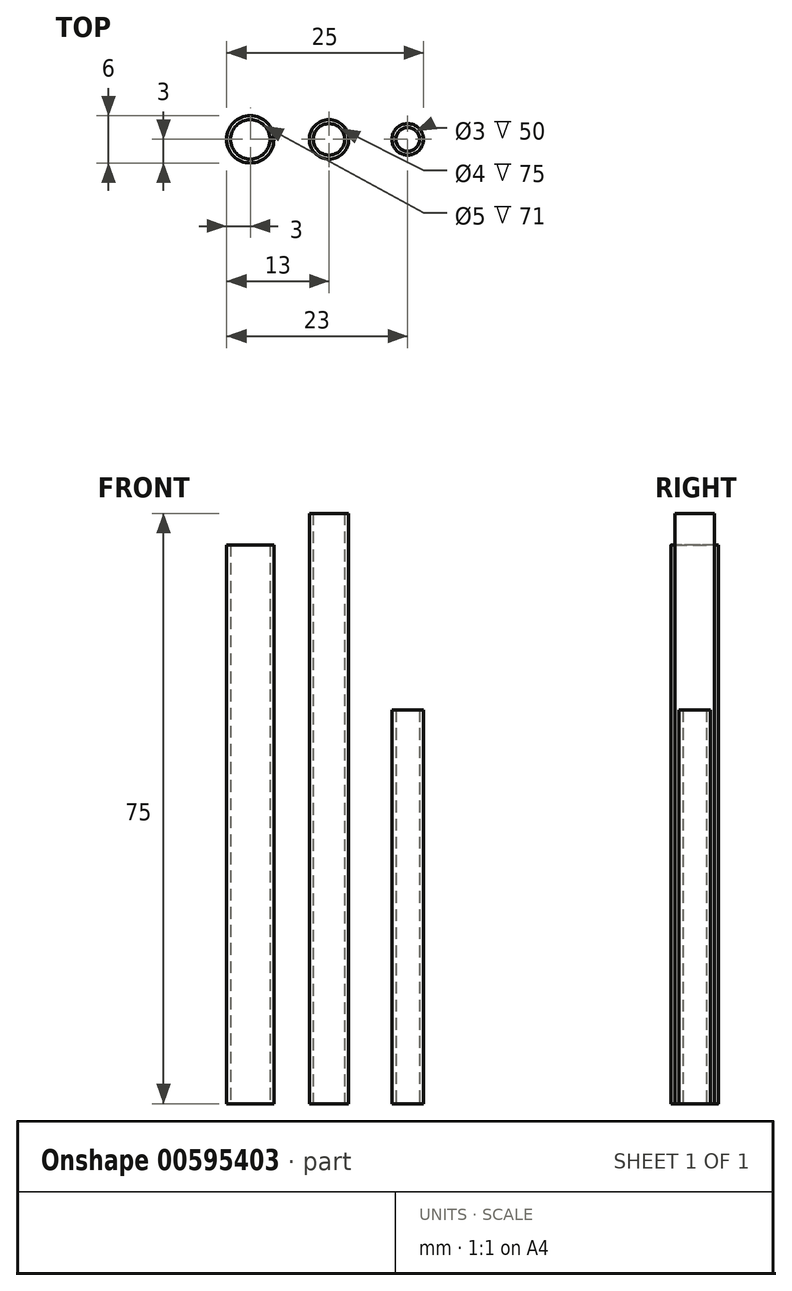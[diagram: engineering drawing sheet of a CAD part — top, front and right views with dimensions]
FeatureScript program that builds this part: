
annotation { "Feature Type Name" : "Feature", "Feature Type Description" : "" }
export const myFeature = defineFeature(function(context is Context, id is Id, definition is map)
    precondition{}
    {
        {
            var Q0;
            Q0=qCreatedBy(makeId("Top.planeOp"),FACE);
            var sketch = newSketch(context, id + "F0", { "sketchPlane" : qUnion([Q0])});
            skCircle(sketch, "E0", {"center": v(-10, 0) * mm, "radius": 3 * mm});
            skCircle(sketch, "E1", {"center": v(-10, 0) * mm, "radius": 2.5 * mm});
            skSolve(sketch);
        }
        {
            var Q0;
            Q0=makeQuery(id+"F0.imprint","IMPRINT",FACE,{"disambiguationData":[TD([[makeQuery(id+"F0.imprint","IMPRINT",EDGE,{"derivedFrom":sQuery(id+"F0.wireOp",EDGE,"E0")}),1.0]])]});
            extrude(context, id + "F1", {"entities" : qUnion([Q0]), "depth" : 71 * mm, "offsetDistance" : 25 * mm});
        }
        {
            var Q0;
            Q0=qCreatedBy(makeId("Top.planeOp"),FACE);
            var sketch = newSketch(context, id + "F2", { "sketchPlane" : qUnion([Q0])});
            skCircle(sketch, "E2", {"center": v(0, 0) * mm, "radius": 2 * mm});
            skCircle(sketch, "E3", {"center": v(0, 0) * mm, "radius": 2.5 * mm});
            skSolve(sketch);
        }
        {
            var Q0;
            Q0=qCreatedBy(makeId("Top.planeOp"),FACE);
            var sketch = newSketch(context, id + "F3", { "sketchPlane" : qUnion([Q0])});
            skCircle(sketch, "E4", {"center": v(10, 0) * mm, "radius": 2 * mm});
            skCircle(sketch, "E5", {"center": v(10, 0) * mm, "radius": 1.5 * mm});
            skSolve(sketch);
        }
        {
            var Q0;
            Q0=makeQuery(id+"F3.imprint","IMPRINT",FACE,{"disambiguationData":[TD([[makeQuery(id+"F3.imprint","IMPRINT",EDGE,{"derivedFrom":sQuery(id+"F3.wireOp",EDGE,"E4")}),1.0]])]});
            extrude(context, id + "F4", {"entities" : qUnion([Q0]), "depth" : 50 * mm, "offsetDistance" : 25 * mm});
        }
        {
            var Q0;
            Q0=makeQuery(id+"F2.imprint","IMPRINT",FACE,{"disambiguationData":[TD([[makeQuery(id+"F2.imprint","IMPRINT",EDGE,{"derivedFrom":sQuery(id+"F2.wireOp",EDGE,"E2")}),-1.0]])]});
            extrude(context, id + "F5", {"entities" : qUnion([Q0]), "depth" : 75 * mm, "offsetDistance" : 25 * mm});
        }
    });
